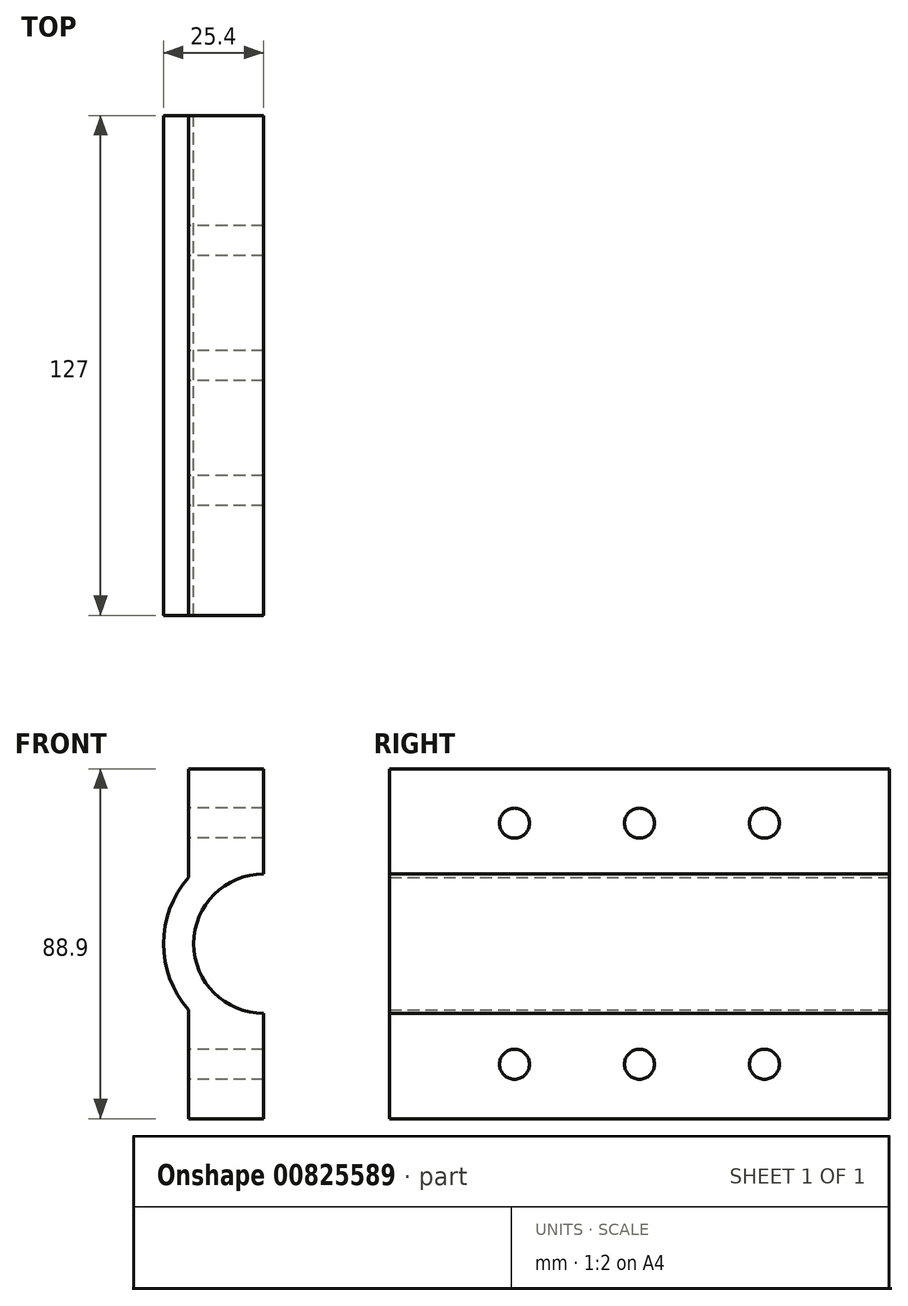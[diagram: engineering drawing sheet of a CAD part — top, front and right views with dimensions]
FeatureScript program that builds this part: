
annotation { "Feature Type Name" : "Feature", "Feature Type Description" : "" }
export const myFeature = defineFeature(function(context is Context, id is Id, definition is map)
    precondition{}
    {
        {
            var Q0;
            Q0=qCreatedBy(makeId("Front.planeOp"),FACE);
            var sketch = newSketch(context, id + "F0", { "sketchPlane" : qUnion([Q0])});
            skArc(sketch, "E0", {"start": v(-19.05, 16.8) * mm, "mid": v(-25.4, 0) * mm, "end": v(-19.05, -16.8) * mm});
            skArc(sketch, "E1", {"start": v(0, 17.72) * mm, "mid": v(-17.72, 0) * mm, "end": v(0, -17.72) * mm});
            skLineSegment(sketch, "E2", {"start": v(0, 0) * mm, "end": v(0, 44.45) * mm});
            skLineSegment(sketch, "E3", {"start": v(0, 44.45) * mm, "end": v(0, -44.45) * mm});
            skLineSegment(sketch, "E4", {"start": v(0, -44.45) * mm, "end": v(-19.05, -44.45) * mm});
            skLineSegment(sketch, "E5", {"start": v(-19.05, -44.45) * mm, "end": v(-19.05, -16.8) * mm});
            skLineSegment(sketch, "E6", {"start": v(0, 44.45) * mm, "end": v(-19.05, 44.45) * mm});
            skLineSegment(sketch, "E7", {"start": v(-19.05, 44.45) * mm, "end": v(-19.05, 16.8) * mm});
            skPoint(sketch, "E8.orphan", {"position": v(0, 25.4) * mm});
            skPoint(sketch, "E9.orphan", {"position": v(0, -25.4) * mm});
            skSolve(sketch);
        }
        {
            var Q0;
            Q0=makeQuery(id+"F0.imprint","IMPRINT",FACE,{"disambiguationData":[TD([[makeQuery(id+"F0.imprint","IMPRINT",EDGE,{"derivedFrom":sQuery(id+"F0.wireOp",EDGE,"E0")}),1.0]])]});
            extrude(context, id + "F1", {"entities" : qUnion([Q0]), "depth" : 127 * mm, "offsetDistance" : 25.4 * mm});
        }
        {
            var Q0;
            Q0=makeQuery(id+"F1.opExtrude","SWEPT_FACE",FACE,{"disambiguationData":[OSD([sQuery(id+"F0.wireOp",EDGE,"E5")])]});
            var sketch = newSketch(context, id + "F2", { "sketchPlane" : qUnion([Q0])});
            skLineSegment(sketch, "E10.bottom", {"start": v(0, -16.8) * mm, "end": v(127, -16.8) * mm, "construction": true});
            skLineSegment(sketch, "E10.top", {"start": v(0, -44.45) * mm, "end": v(127, -44.45) * mm, "construction": true});
            skLineSegment(sketch, "E10.left", {"start": v(0, -16.8) * mm, "end": v(0, -44.45) * mm, "construction": true});
            skLineSegment(sketch, "E10.right", {"start": v(127, -16.8) * mm, "end": v(127, -44.45) * mm, "construction": true});
            skLineSegment(sketch, "E11", {"start": v(63.5, -16.8) * mm, "end": v(63.5, -44.45) * mm});
            skLineSegment(sketch, "E12", {"start": v(31.75, -16.8) * mm, "end": v(31.75, -44.45) * mm});
            skPoint(sketch, "E12.startSnap0", {"position": v(31.75, -30.63) * mm});
            skCircle(sketch, "E13", {"center": v(31.75, -30.63) * mm, "radius": 3.81 * mm});
            skPoint(sketch, "E14.orphan", {"position": v(0, -30.63) * mm});
            skCircle(sketch, "E15", {"center": v(63.5, -30.63) * mm, "radius": 3.81 * mm});
            skCircle(sketch, "E16", {"center": v(95.25, -30.63) * mm, "radius": 3.81 * mm});
            skPoint(sketch, "E17.start.orphan", {"position": v(127, -30.63) * mm});
            skLineSegment(sketch, "E18", {"start": v(95.25, -16.8) * mm, "end": v(95.25, -44.45) * mm});
            skSolve(sketch);
        }
        {
            var Q0;
            Q0 = qSketchRegion(id + "F2", true);
            extrude(context, id + "F3", {"entities" : qUnion([Q0]), "operationType" : NewBodyOperationType.REMOVE, "oppositeDirection" : true, "depth" : 25.4 * mm, "offsetDistance" : 25.4 * mm});
        }
        {
            var Q0;
            Q0=makeQuery(id+"F1.opExtrude","SWEPT_FACE",FACE,{"disambiguationData":[OSD([sQuery(id+"F0.wireOp",EDGE,"E7")])]});
            var sketch = newSketch(context, id + "F4", { "sketchPlane" : qUnion([Q0])});
            skLineSegment(sketch, "E19", {"start": v(0, 30.63) * mm, "end": v(127, 30.63) * mm, "construction": true});
            skCircle(sketch, "E20", {"center": v(63.5, 30.63) * mm, "radius": 3.81 * mm});
            skLineSegment(sketch, "E21", {"start": v(63.5, 44.45) * mm, "end": v(63.5, 16.8) * mm});
            skLineSegment(sketch, "E22", {"start": v(0, 44.45) * mm, "end": v(63.5, 44.45) * mm});
            skLineSegment(sketch, "E23", {"start": v(127, 44.45) * mm, "end": v(63.5, 44.45) * mm});
            skCircle(sketch, "E24", {"center": v(31.75, 30.63) * mm, "radius": 3.81 * mm});
            skPoint(sketch, "E24.centerSnap0", {"position": v(31.75, 44.45) * mm});
            skCircle(sketch, "E25", {"center": v(95.25, 30.63) * mm, "radius": 3.81 * mm});
            skPoint(sketch, "E25.centerSnap0", {"position": v(95.25, 44.45) * mm});
            skSolve(sketch);
        }
        {
            var Q0;
            Q0 = qSketchRegion(id + "F4", true);
            extrude(context, id + "F5", {"entities" : qUnion([Q0]), "operationType" : NewBodyOperationType.REMOVE, "oppositeDirection" : true, "depth" : 25.4 * mm, "offsetDistance" : 25.4 * mm});
        }
    });
